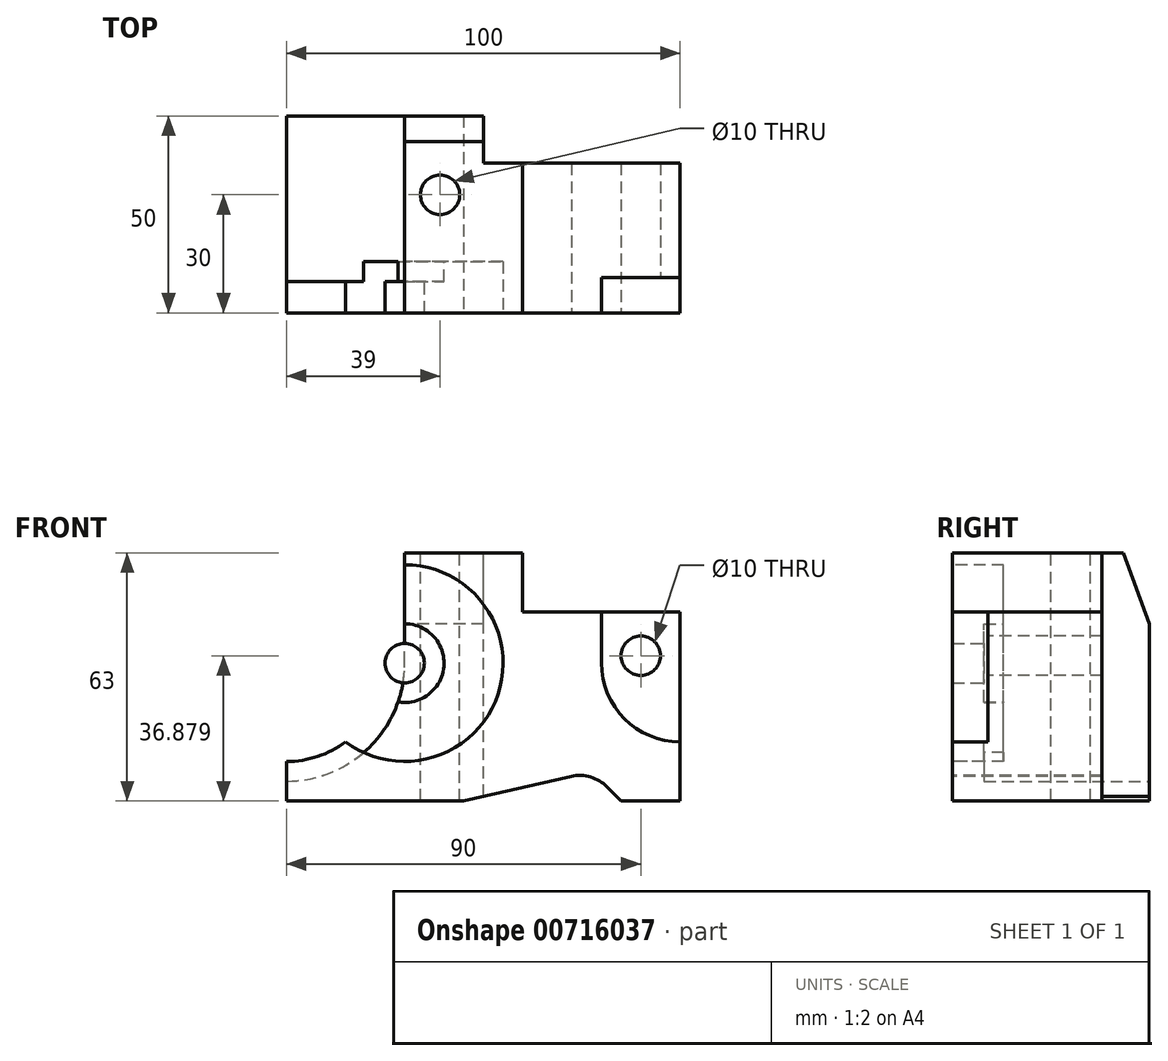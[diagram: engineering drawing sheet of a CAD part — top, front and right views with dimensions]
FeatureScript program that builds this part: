
annotation { "Feature Type Name" : "Feature", "Feature Type Description" : "" }
export const myFeature = defineFeature(function(context is Context, id is Id, definition is map)
    precondition{}
    {
        {
            var Q0;
            Q0=qCreatedBy(makeId("Front.planeOp"),FACE);
            var sketch = newSketch(context, id + "F0", { "sketchPlane" : qUnion([Q0])});
            skLineSegment(sketch, "E0.bottom", {"start": v(-50, -31.5) * mm, "end": v(50, -31.5) * mm});
            skLineSegment(sketch, "E0.top", {"start": v(-50, 31.5) * mm, "end": v(50, 31.5) * mm});
            skLineSegment(sketch, "E0.left", {"start": v(-50, -31.5) * mm, "end": v(-50, 31.5) * mm});
            skLineSegment(sketch, "E0.right", {"start": v(50, -31.5) * mm, "end": v(50, 31.5) * mm});
            skPoint(sketch, "E0.middle", {"position": v(0, 0) * mm});
            skLineSegment(sketch, "E1", {"start": v(50, 31.5) * mm, "end": v(10, 31.5) * mm});
            skLineSegment(sketch, "E2", {"start": v(10, 31.5) * mm, "end": v(10, 16.5) * mm});
            skLineSegment(sketch, "E3", {"start": v(10, 16.5) * mm, "end": v(50, 16.5) * mm});
            skLineSegment(sketch, "E4", {"start": v(50, 16.5) * mm, "end": v(50, 31.5) * mm});
            skSolve(sketch);
        }
        {
            var Q0;
            Q0=makeQuery(id+"F0.imprint","IMPRINT",FACE,{"disambiguationData":[TD([[makeQuery(id+"F0.imprint","IMPRINT",EDGE,{"derivedFrom":sQuery(id+"F0.wireOp",EDGE,"E0.bottom")}),1.0]])]});
            extrude(context, id + "F1", {"entities" : qUnion([Q0]), "depth" : 50 * mm, "offsetDistance" : 25 * mm});
        }
        {
            var Q0;
            Q0=makeQuery(id+"F1.opExtrude","CAP_FACE",FACE,{"disambiguationData":[OSD([sQuery(id+"F0.wireOp",EDGE,"E0.bottom"),sQuery(id+"F0.wireOp",EDGE,"E0.top"),sQuery(id+"F0.wireOp",EDGE,"E0.left"),sQuery(id+"F0.wireOp",EDGE,"E0.right"),sQuery(id+"F0.wireOp",EDGE,"E2"),sQuery(id+"F0.wireOp",EDGE,"E3")])],"isStart":false});
            var sketch = newSketch(context, id + "F2", { "sketchPlane" : qUnion([Q0])});
            skLineSegment(sketch, "E5", {"start": v(50, -31.5) * mm, "end": v(50, 3.5) * mm});
            skCircle(sketch, "E6", {"center": v(50, 3.5) * mm, "radius": 20 * mm});
            skLineSegment(sketch, "E7", {"start": v(30, 3.5) * mm, "end": v(30, 32.67) * mm});
            skSolve(sketch);
        }
        {
            var Q0;
            Q0 = qSketchRegion(id + "F2", true);
            var Q1;
            {var subQ0=sQuery(id+"F2.wireOp",EDGE,"E7");var subQ1=sQuery(id+"F2.wireOp",EDGE,"E6");var subQ2=makeQuery(id+"F2.imprint","INTERSECT",VERTEX,{"derivedFrom":[subQ1,subQ0]});Q1=makeQuery(id+"F2.imprint","IMPRINT",FACE,{"disambiguationData":[TD([[makeQuery(id+"F2.imprint","IMPRINT",EDGE,{"disambiguationData":[TD([[subQ2,1.0]])],"derivedFrom":subQ1}),-1.0]])]});}
            extrude(context, id + "F3", {"entities" : qUnion([Q0, Q1]), "operationType" : NewBodyOperationType.REMOVE, "oppositeDirection" : true, "depth" : 9 * mm, "offsetDistance" : 25 * mm});
        }
        {
            var Q0;
            Q0=makeQuery(id+"F3.boolean.opBoolean","COPY",FACE,{"derivedFrom":makeQuery(id+"F3.opExtrude","CAP_FACE",FACE,{"disambiguationData":[OSD([sQuery(id+"F0.wireOp",EDGE,"E3"),sQuery(id+"F2.wireOp",EDGE,"E6"),sQuery(id+"F2.wireOp",EDGE,"E7")])],"isStart":false})});
            var sketch = newSketch(context, id + "F4", { "sketchPlane" : qUnion([Q0])});
            skCircle(sketch, "E8", {"center": v(40, 5.38) * mm, "radius": 5 * mm});
            skSolve(sketch);
        }
        {
            var Q0;
            Q0 = qSketchRegion(id + "F4", true);
            extrude(context, id + "F5", {"entities" : qUnion([Q0]), "operationType" : NewBodyOperationType.REMOVE, "oppositeDirection" : true, "depth" : 100 * mm, "offsetDistance" : 25 * mm});
        }
        {
            var Q0;
            Q0=makeQuery(id+"F1.opExtrude","CAP_FACE",FACE,{"disambiguationData":[OSD([sQuery(id+"F0.wireOp",EDGE,"E0.bottom"),sQuery(id+"F0.wireOp",EDGE,"E0.top"),sQuery(id+"F0.wireOp",EDGE,"E0.left"),sQuery(id+"F0.wireOp",EDGE,"E0.right"),sQuery(id+"F0.wireOp",EDGE,"E2"),sQuery(id+"F0.wireOp",EDGE,"E3")])],"isStart":false});
            var sketch = newSketch(context, id + "F6", { "sketchPlane" : qUnion([Q0])});
            skLineSegment(sketch, "E9", {"start": v(-50, -31.5) * mm, "end": v(-50, 3.5) * mm});
            skCircle(sketch, "E10", {"center": v(-50, 3.5) * mm, "radius": 25 * mm});
            skLineSegment(sketch, "E11", {"start": v(-25, 3.5) * mm, "end": v(-25, 38.94) * mm});
            skSolve(sketch);
        }
        {
            var Q0;
            Q0 = qSketchRegion(id + "F6", true);
            var Q1;
            {var subQ0=sQuery(id+"F6.wireOp",EDGE,"E11");var subQ1=sQuery(id+"F6.wireOp",EDGE,"E10");var subQ2=makeQuery(id+"F6.imprint","INTERSECT",VERTEX,{"derivedFrom":[subQ1,subQ0]});Q1=makeQuery(id+"F6.imprint","IMPRINT",FACE,{"disambiguationData":[TD([[makeQuery(id+"F6.imprint","IMPRINT",EDGE,{"disambiguationData":[TD([[subQ2,-1.0]])],"derivedFrom":subQ1}),-1.0]])]});}
            extrude(context, id + "F7", {"entities" : qUnion([Q0, Q1]), "operationType" : NewBodyOperationType.REMOVE, "oppositeDirection" : true, "depth" : 8 * mm, "offsetDistance" : 25 * mm});
        }
        {
            var Q0;
            Q0=makeQuery(id+"F1.opExtrude","CAP_FACE",FACE,{"disambiguationData":[OSD([sQuery(id+"F0.wireOp",EDGE,"E0.bottom"),sQuery(id+"F0.wireOp",EDGE,"E0.top"),sQuery(id+"F0.wireOp",EDGE,"E0.left"),sQuery(id+"F0.wireOp",EDGE,"E0.right"),sQuery(id+"F0.wireOp",EDGE,"E2"),sQuery(id+"F0.wireOp",EDGE,"E3")])],"isStart":true});
            var sketch = newSketch(context, id + "F8", { "sketchPlane" : qUnion([Q0])});
            skLineSegment(sketch, "E12", {"start": v(50, -31.5) * mm, "end": v(50, 3.5) * mm});
            skCircle(sketch, "E13", {"center": v(50, 3.5) * mm, "radius": 30 * mm});
            skLineSegment(sketch, "E14", {"start": v(20, 3.5) * mm, "end": v(20, 39.43) * mm});
            skSolve(sketch);
        }
        {
            var Q0;
            Q0 = qSketchRegion(id + "F8", true);
            var Q1;
            {var subQ0=sQuery(id+"F8.wireOp",EDGE,"E14");var subQ1=sQuery(id+"F8.wireOp",EDGE,"E13");var subQ2=makeQuery(id+"F8.imprint","INTERSECT",VERTEX,{"derivedFrom":[subQ1,subQ0]});Q1=makeQuery(id+"F8.imprint","IMPRINT",FACE,{"disambiguationData":[TD([[makeQuery(id+"F8.imprint","IMPRINT",EDGE,{"disambiguationData":[TD([[subQ2,1.0]])],"derivedFrom":subQ1}),-1.0]])]});}
            extrude(context, id + "F9", {"entities" : qUnion([Q0, Q1]), "operationType" : NewBodyOperationType.REMOVE, "oppositeDirection" : true, "depth" : 42 * mm, "offsetDistance" : 25 * mm});
        }
        {
            var Q0;
            Q0=makeQuery(id+"F1.opExtrude","CAP_FACE",FACE,{"disambiguationData":[OSD([sQuery(id+"F0.wireOp",EDGE,"E0.bottom"),sQuery(id+"F0.wireOp",EDGE,"E0.top"),sQuery(id+"F0.wireOp",EDGE,"E0.left"),sQuery(id+"F0.wireOp",EDGE,"E0.right"),sQuery(id+"F0.wireOp",EDGE,"E2"),sQuery(id+"F0.wireOp",EDGE,"E3")])],"isStart":false});
            var sketch = newSketch(context, id + "F10", { "sketchPlane" : qUnion([Q0])});
            skLineSegment(sketch, "E15", {"start": v(-20, -31.5) * mm, "end": v(-20, 3.5) * mm});
            skCircle(sketch, "E16", {"center": v(-20, 3.5) * mm, "radius": 25 * mm});
            skSolve(sketch);
        }
        {
            var Q0;
            Q0 = qSketchRegion(id + "F10", true);
            extrude(context, id + "F11", {"entities" : qUnion([Q0]), "operationType" : NewBodyOperationType.REMOVE, "oppositeDirection" : true, "depth" : 13 * mm, "offsetDistance" : 25 * mm});
        }
        {
            var Q0;
            {var subQ0=sQuery(id+"F0.wireOp",EDGE,"E0.top");var subQ1=sQuery(id+"F8.wireOp",EDGE,"E14");Q0=makeQuery(id+"F11.boolean.opBoolean","SPLIT",FACE,{"disambiguationData":[TD([makeQuery(id+"F1.opExtrude","SWEPT_FACE",FACE,{"disambiguationData":[OSD([subQ0])]})])],"derivedFrom":makeQuery(id+"F9.boolean.opBoolean","COPY",FACE,{"derivedFrom":makeQuery(id+"F9.opExtrude","CAP_FACE",FACE,{"disambiguationData":[OSD([subQ0,sQuery(id+"F8.wireOp",EDGE,"E13"),subQ1])],"isStart":false})})});}
            var sketch = newSketch(context, id + "F12", { "sketchPlane" : qUnion([Q0])});
            skLineSegment(sketch, "E17", {"start": v(20, 31.5) * mm, "end": v(20, 27.84) * mm});
            skLineSegment(sketch, "E18", {"start": v(20, 27.84) * mm, "end": v(25.5, 27.84) * mm});
            skLineSegment(sketch, "E19", {"start": v(25.5, 27.84) * mm, "end": v(25.5, 31.5) * mm});
            skLineSegment(sketch, "E20", {"start": v(25.5, 31.5) * mm, "end": v(20, 31.5) * mm});
            skSolve(sketch);
        }
        {
            var Q0;
            Q0 = qSketchRegion(id + "F12", true);
            extrude(context, id + "F13", {"entities" : qUnion([Q0]), "operationType" : NewBodyOperationType.REMOVE, "oppositeDirection" : true, "depth" : 25 * mm, "offsetDistance" : 25 * mm});
        }
        {
            var Q0;
            Q0=makeQuery(id+"F11.boolean.opBoolean","COPY",FACE,{"derivedFrom":makeQuery(id+"F11.opExtrude","CAP_FACE",FACE,{"disambiguationData":[OSD([sQuery(id+"F10.wireOp",EDGE,"E16")])],"isStart":false})});
            var sketch = newSketch(context, id + "F14", { "sketchPlane" : qUnion([Q0])});
            skArc(sketch, "E21", {"start": v(-21.67, -6.36) * mm, "mid": v(-10.04, 2.66) * mm, "end": v(-20, 13.5) * mm});
            skSolve(sketch);
        }
        {
            var Q0;
            Q0 = qSketchRegion(id + "F14", true);
            var Q1;
            {var subQ0=sQuery(id+"F14.wireOp",EDGE,"E21");Q1=makeQuery(id+"F14.imprint","IMPRINT",FACE,{"disambiguationData":[TD([[makeQuery(id+"F14.imprint","IMPRINT",EDGE,{"derivedFrom":subQ0}),1.0]])]});}
            extrude(context, id + "F15", {"entities" : qUnion([Q0, Q1]), "operationType" : NewBodyOperationType.ADD, "depth" : 5 * mm, "offsetDistance" : 25 * mm});
        }
        {
            var Q0;
            Q0=makeQuery(id+"F15.opExtrude","CAP_FACE",FACE,{"disambiguationData":[OSD([sQuery(id+"F8.wireOp",EDGE,"E13"),sQuery(id+"F8.wireOp",EDGE,"E14"),sQuery(id+"F10.wireOp",EDGE,"E16"),sQuery(id+"F14.wireOp",EDGE,"E21")])],"isStart":false});
            var sketch = newSketch(context, id + "F16", { "sketchPlane" : qUnion([Q0])});
            skCircle(sketch, "E22", {"center": v(-20, 3.5) * mm, "radius": 5 * mm});
            skSolve(sketch);
        }
        {
            var Q0;
            Q0 = qSketchRegion(id + "F16", true);
            extrude(context, id + "F17", {"entities" : qUnion([Q0]), "operationType" : NewBodyOperationType.ADD, "depth" : 8 * mm, "offsetDistance" : 25 * mm});
        }
        {
            var Q0;
            {var subQ0=sQuery(id+"F8.wireOp",EDGE,"E14");Q0=makeQuery(id+"F15.boolean.opBoolean","MERGE",FACE,{"derivedFrom":[makeQuery(id+"F13.boolean.opBoolean","MERGE",FACE,{"derivedFrom":[makeQuery(id+"F9.boolean.opBoolean","COPY",FACE,{"derivedFrom":makeQuery(id+"F9.opExtrude","SWEPT_FACE",FACE,{"disambiguationData":[OSD([subQ0])]})}),makeQuery(id+"F13.opExtrude","SWEPT_FACE",FACE,{"disambiguationData":[OSD([sQuery(id+"F12.wireOp",EDGE,"E17")])]})]}),makeQuery(id+"F15.opExtrude","SWEPT_FACE",FACE,{"disambiguationData":[OSD([subQ0,sQuery(id+"F10.wireOp",EDGE,"E16")])]})]});}
            var sketch = newSketch(context, id + "F18", { "sketchPlane" : qUnion([Q0])});
            skLineSegment(sketch, "E23", {"start": v(0, 13.5) * mm, "end": v(6.55, 31.5) * mm});
            skSolve(sketch);
        }
        {
            var Q0;
            Q0 = qSketchRegion(id + "F18", true);
            var Q1;
            {var subQ0=sQuery(id+"F18.wireOp",EDGE,"E23");Q1=makeQuery(id+"F18.imprint","IMPRINT",FACE,{"disambiguationData":[TD([[makeQuery(id+"F18.imprint","IMPRINT",EDGE,{"derivedFrom":subQ0}),1.0]])]});}
            extrude(context, id + "F19", {"entities" : qUnion([Q0, Q1]), "operationType" : NewBodyOperationType.REMOVE, "endBound" : BoundingType.THROUGH_ALL, "oppositeDirection" : true, "depth" : 25 * mm, "offsetDistance" : 25 * mm});
        }
        {
            var Q0;
            Q0=makeQuery(id+"F1.opExtrude","SWEPT_FACE",FACE,{"disambiguationData":[OSD([sQuery(id+"F0.wireOp",EDGE,"E0.top")])]});
            var sketch = newSketch(context, id + "F20", { "sketchPlane" : qUnion([Q0])});
            skLineSegment(sketch, "E24", {"start": v(50, -12) * mm, "end": v(50, 0) * mm});
            skLineSegment(sketch, "E25", {"start": v(50, 0) * mm, "end": v(0, 0) * mm});
            skLineSegment(sketch, "E26", {"start": v(50, -12) * mm, "end": v(0, -12) * mm});
            skLineSegment(sketch, "E27", {"start": v(0, -12) * mm, "end": v(0, 0) * mm});
            skSolve(sketch);
        }
        {
            var Q0;
            Q0 = qSketchRegion(id + "F20", true);
            extrude(context, id + "F21", {"entities" : qUnion([Q0]), "operationType" : NewBodyOperationType.REMOVE, "endBound" : BoundingType.THROUGH_ALL, "oppositeDirection" : true, "depth" : 25 * mm, "offsetDistance" : 25 * mm});
        }
        {
            var Q0;
            Q0=makeQuery(id+"F1.opExtrude","SWEPT_FACE",FACE,{"disambiguationData":[OSD([sQuery(id+"F0.wireOp",EDGE,"E0.top")])]});
            var sketch = newSketch(context, id + "F22", { "sketchPlane" : qUnion([Q0])});
            skCircle(sketch, "E28", {"center": v(-11, -20) * mm, "radius": 5 * mm});
            skSolve(sketch);
        }
        {
            var Q0;
            Q0 = qSketchRegion(id + "F22", true);
            extrude(context, id + "F23", {"entities" : qUnion([Q0]), "operationType" : NewBodyOperationType.REMOVE, "endBound" : BoundingType.THROUGH_ALL, "oppositeDirection" : true, "depth" : 25 * mm, "offsetDistance" : 25 * mm});
        }
        {
            var Q0;
            Q0=makeQuery(id+"F1.opExtrude","CAP_FACE",FACE,{"disambiguationData":[OSD([sQuery(id+"F0.wireOp",EDGE,"E0.bottom"),sQuery(id+"F0.wireOp",EDGE,"E0.top"),sQuery(id+"F0.wireOp",EDGE,"E0.left"),sQuery(id+"F0.wireOp",EDGE,"E0.right"),sQuery(id+"F0.wireOp",EDGE,"E2"),sQuery(id+"F0.wireOp",EDGE,"E3")])],"isStart":false});
            var sketch = newSketch(context, id + "F24", { "sketchPlane" : qUnion([Q0])});
            skLineSegment(sketch, "E29", {"start": v(-5, -31.5) * mm, "end": v(22.34, -25.23) * mm});
            skLineSegment(sketch, "E30", {"start": v(35, -31.5) * mm, "end": v(31.45, -27.95) * mm});
            skArc(sketch, "E31", {"start": v(31.45, -27.95) * mm, "mid": v(27.24, -25.44) * mm, "end": v(22.34, -25.23) * mm});
            skLineSegment(sketch, "E32", {"start": v(-5, -31.5) * mm, "end": v(35, -31.5) * mm});
            skSolve(sketch);
        }
        {
            var Q0;
            Q0=makeQuery(id+"F24.imprint","IMPRINT",FACE,{"disambiguationData":[TD([[makeQuery(id+"F24.imprint","IMPRINT",EDGE,{"derivedFrom":sQuery(id+"F24.wireOp",EDGE,"E29")}),-1.0]])]});
            extrude(context, id + "F25", {"entities" : qUnion([Q0]), "operationType" : NewBodyOperationType.REMOVE, "endBound" : BoundingType.THROUGH_ALL, "oppositeDirection" : true, "depth" : 25 * mm, "offsetDistance" : 25 * mm});
        }
    });
